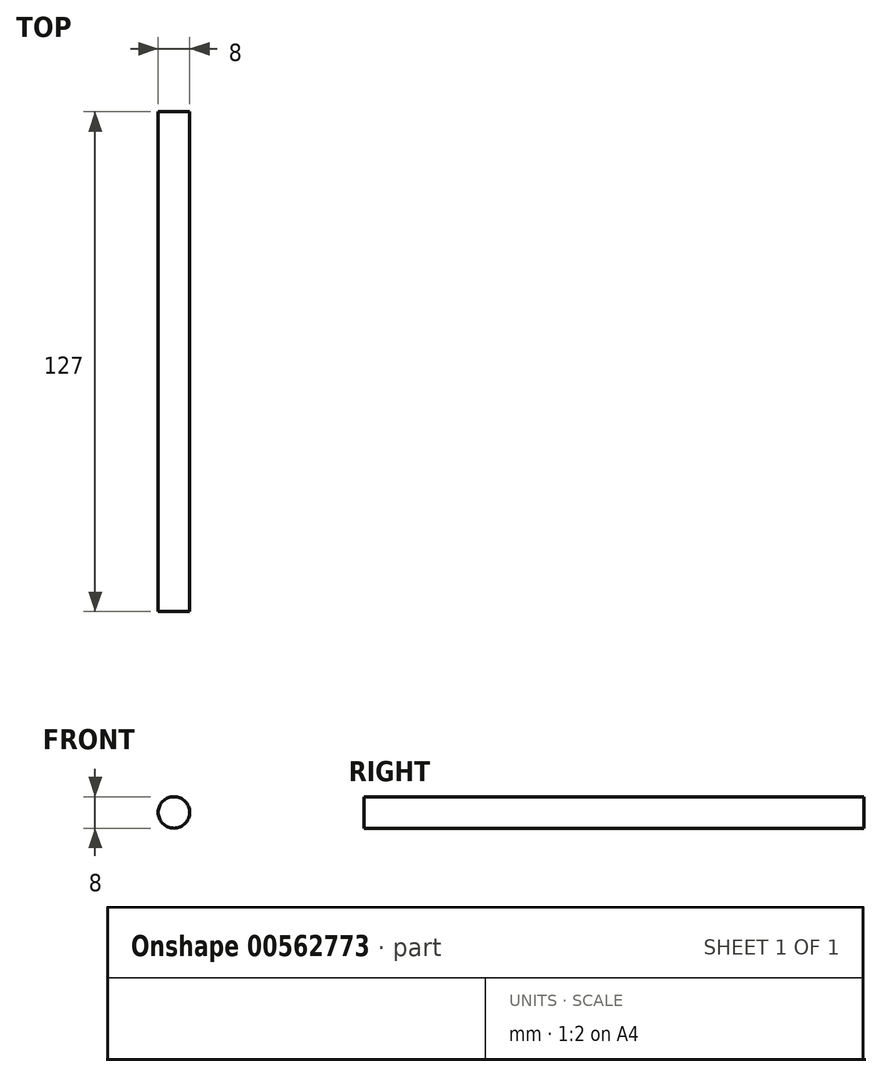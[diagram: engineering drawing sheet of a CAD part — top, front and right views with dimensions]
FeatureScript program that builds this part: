
annotation { "Feature Type Name" : "Feature", "Feature Type Description" : "" }
export const myFeature = defineFeature(function(context is Context, id is Id, definition is map)
    precondition{}
    {
        {
            var Q0;
            Q0=qCreatedBy(makeId("Front.planeOp"),FACE);
            var sketch = newSketch(context, id + "F0", { "sketchPlane" : qUnion([Q0])});
            skCircle(sketch, "E0", {"center": v(0, 0) * mm, "radius": 4 * mm});
            skSolve(sketch);
        }
        {
            var Q0;
            Q0 = qSketchRegion(id + "F0", true);
            extrude(context, id + "F1", {"entities" : qUnion([Q0]), "depth" : 127 * mm, "offsetDistance" : 25.4 * mm});
        }
    });
